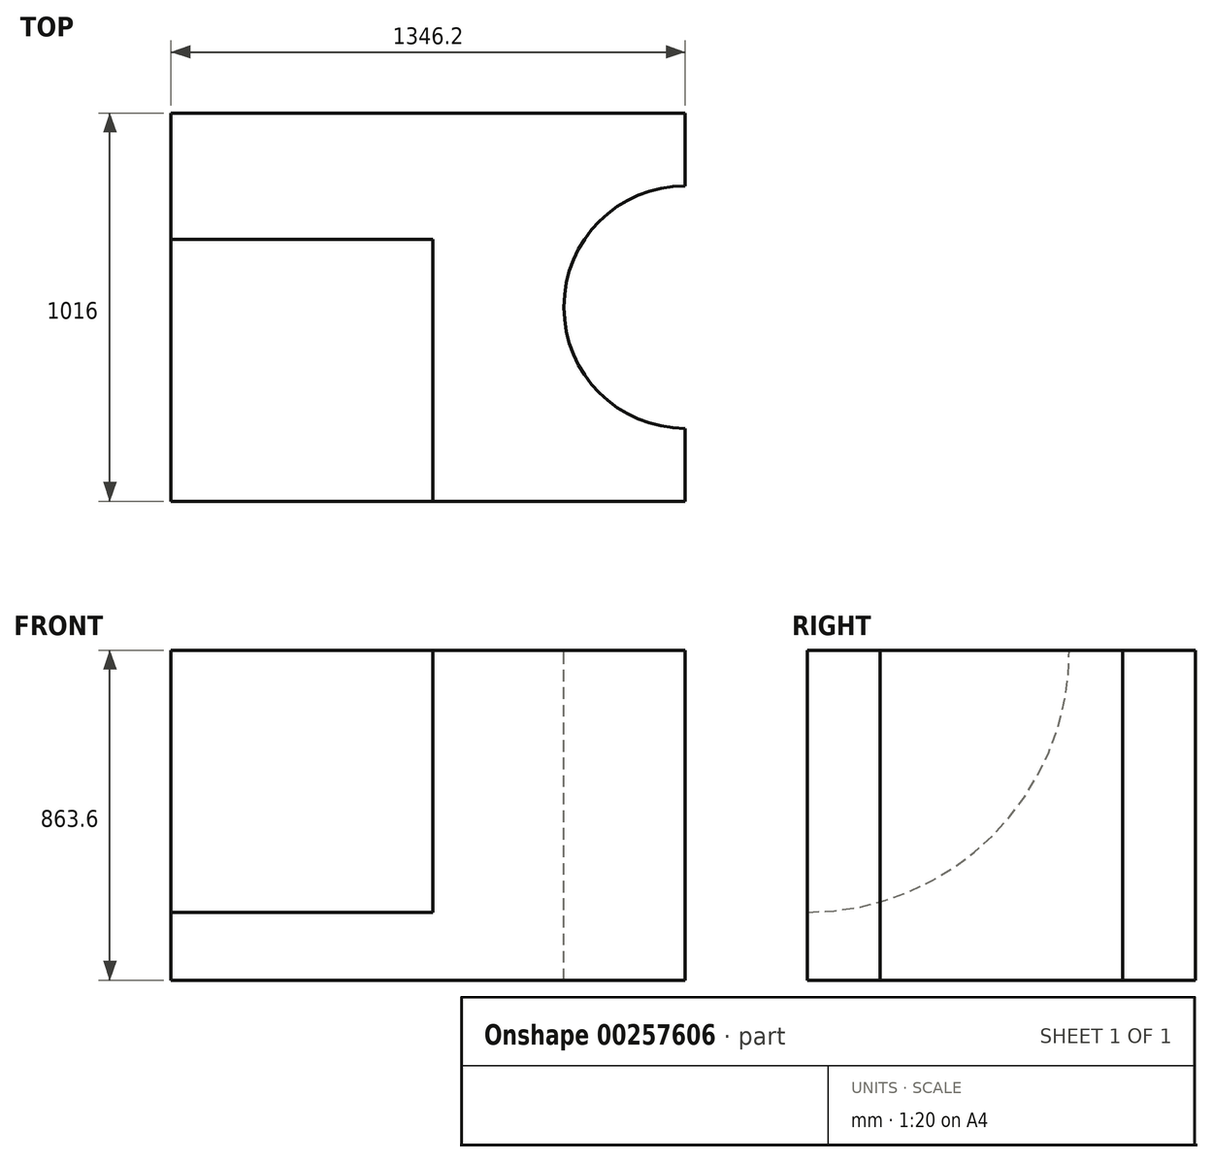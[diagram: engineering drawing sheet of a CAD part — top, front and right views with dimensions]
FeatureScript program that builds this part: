
annotation { "Feature Type Name" : "Feature", "Feature Type Description" : "" }
export const myFeature = defineFeature(function(context is Context, id is Id, definition is map)
    precondition{}
    {
        {
            var Q0;
            Q0=qCreatedBy(makeId("Front.planeOp"),FACE);
            var sketch = newSketch(context, id + "F0", { "sketchPlane" : qUnion([Q0])});
            skLineSegment(sketch, "E0.bottom", {"start": v(-670.8, 452.6) * mm, "end": v(675.4, 452.6) * mm});
            skLineSegment(sketch, "E0.top", {"start": v(-670.8, -411) * mm, "end": v(675.4, -411) * mm});
            skLineSegment(sketch, "E0.left", {"start": v(-670.8, 452.6) * mm, "end": v(-670.8, -411) * mm});
            skLineSegment(sketch, "E0.right", {"start": v(675.4, 452.6) * mm, "end": v(675.4, -411) * mm});
            skSolve(sketch);
        }
        {
            var Q0;
            Q0 = qSketchRegion(id + "F0", true);
            extrude(context, id + "F1", {"entities" : qUnion([Q0]), "depth" : 1016 * mm});
        }
        {
            var Q0;
            Q0=makeQuery(id+"F1.opExtrude","SWEPT_FACE",FACE,{"disambiguationData":[OSD([sQuery(id+"F0.wireOp",EDGE,"E0.bottom")])]});
            var sketch = newSketch(context, id + "F2", { "sketchPlane" : qUnion([Q0])});
            skCircle(sketch, "E1", {"center": v(675.4, -508) * mm, "radius": 317.5 * mm});
            skSolve(sketch);
        }
        {
            var Q0;
            Q0 = qSketchRegion(id + "F2", true);
            extrude(context, id + "F3", {"entities" : qUnion([Q0]), "operationType" : NewBodyOperationType.REMOVE, "oppositeDirection" : true, "depth" : 863.6 * mm});
        }
        {
            var Q0;
            Q0=makeQuery(id+"F1.opExtrude","SWEPT_FACE",FACE,{"disambiguationData":[OSD([sQuery(id+"F0.wireOp",EDGE,"E0.left")])]});
            var sketch = newSketch(context, id + "F4", { "sketchPlane" : qUnion([Q0])});
            skCircle(sketch, "E2", {"center": v(1016, 452.6) * mm, "radius": 685.8 * mm});
            skSolve(sketch);
        }
        {
            var Q0;
            Q0 = qSketchRegion(id + "F4", true);
            extrude(context, id + "F5", {"entities" : qUnion([Q0]), "operationType" : NewBodyOperationType.REMOVE, "oppositeDirection" : true, "depth" : 685.8 * mm});
        }
    });
